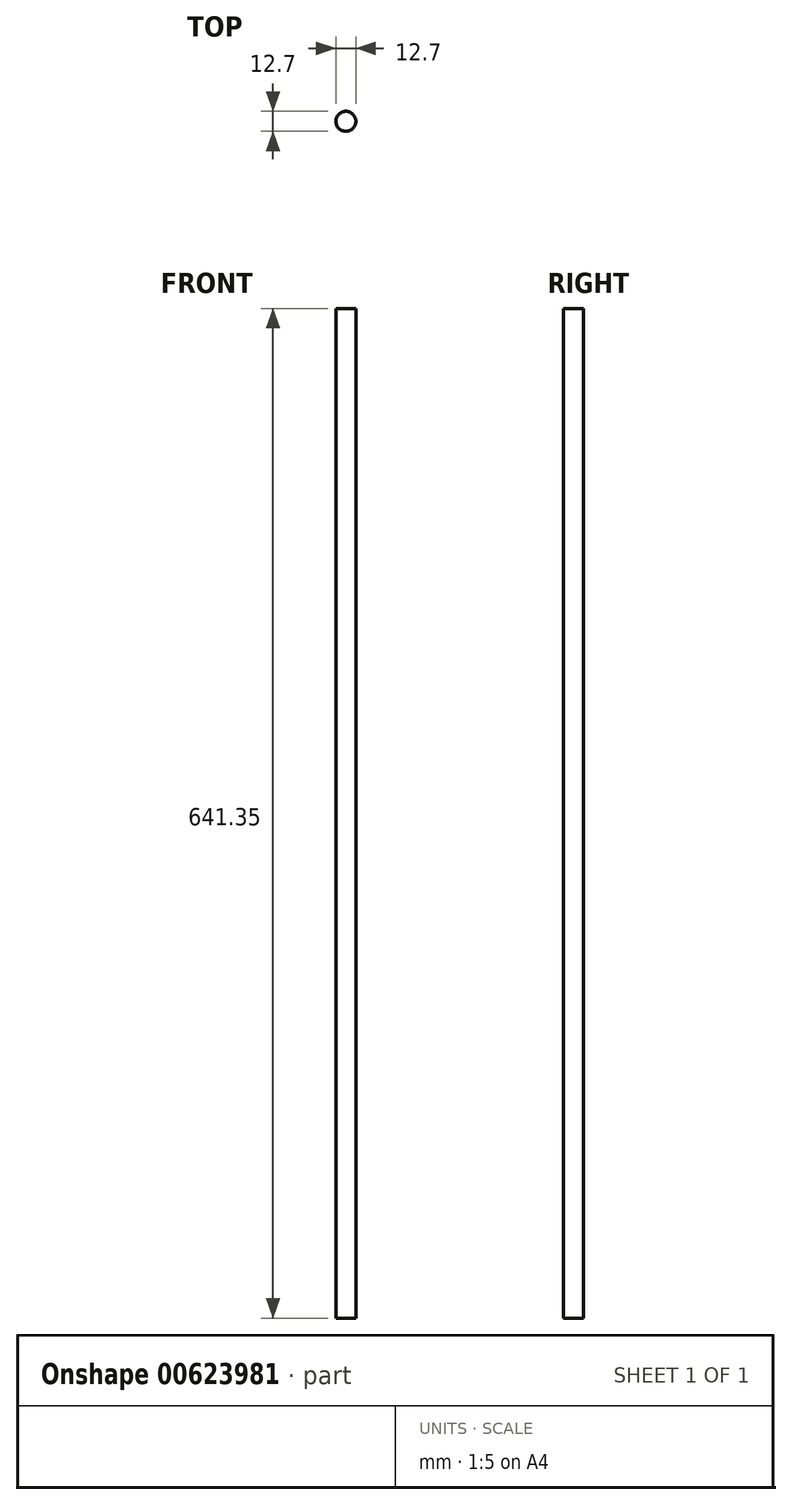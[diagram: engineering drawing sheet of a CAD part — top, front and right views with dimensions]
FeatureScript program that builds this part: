
annotation { "Feature Type Name" : "Feature", "Feature Type Description" : "" }
export const myFeature = defineFeature(function(context is Context, id is Id, definition is map)
    precondition{}
    {
        {
            var Q0;
            Q0=qCreatedBy(makeId("Top.planeOp"),FACE);
            var sketch = newSketch(context, id + "F0", { "sketchPlane" : qUnion([Q0])});
            skCircle(sketch, "E0", {"center": v(0, 0) * mm, "radius": 6.35 * mm});
            skSolve(sketch);
        }
        {
            var Q0;
            Q0=makeQuery(id+"F0.imprint","IMPRINT",FACE,{"disambiguationData":[TD([[makeQuery(id+"F0.imprint","IMPRINT",EDGE,{"derivedFrom":sQuery(id+"F0.wireOp",EDGE,"E0")}),1.0]])]});
            extrude(context, id + "F1", {"entities" : qUnion([Q0]), "depth" : 660.4 * mm, "offsetDistance" : 25.4 * mm});
        }
        {
            var Q0;
            Q0=makeQuery(id+"F1.opExtrude","CAP_FACE",FACE,{"disambiguationData":[OSD([sQuery(id+"F0.wireOp",EDGE,"E0")])],"isStart":false});
            extrude(context, id + "F2", {"entities" : qUnion([Q0]), "operationType" : NewBodyOperationType.REMOVE, "oppositeDirection" : true, "depth" : 51.72 * mm, "offsetDistance" : 25.4 * mm});
        }
        {
            var Q0;
            Q0=makeQuery(id+"F2.boolean.opBoolean","COPY",FACE,{"derivedFrom":makeQuery(id+"F2.opExtrude","CAP_FACE",FACE,{"disambiguationData":[OSD([sQuery(id+"F0.wireOp",EDGE,"E0")])],"isStart":false})});
            extrude(context, id + "F3", {"entities" : qUnion([Q0]), "operationType" : NewBodyOperationType.ADD, "depth" : 16.33 * mm, "offsetDistance" : 25.4 * mm});
        }
        {
            var Q0;
            Q0=makeQuery(id+"F1.opExtrude","CAP_FACE",FACE,{"disambiguationData":[OSD([sQuery(id+"F0.wireOp",EDGE,"E0")])],"isStart":true});
            extrude(context, id + "F4", {"entities" : qUnion([Q0]), "operationType" : NewBodyOperationType.ADD, "depth" : 16.33 * mm, "offsetDistance" : 25.4 * mm});
        }
    });
